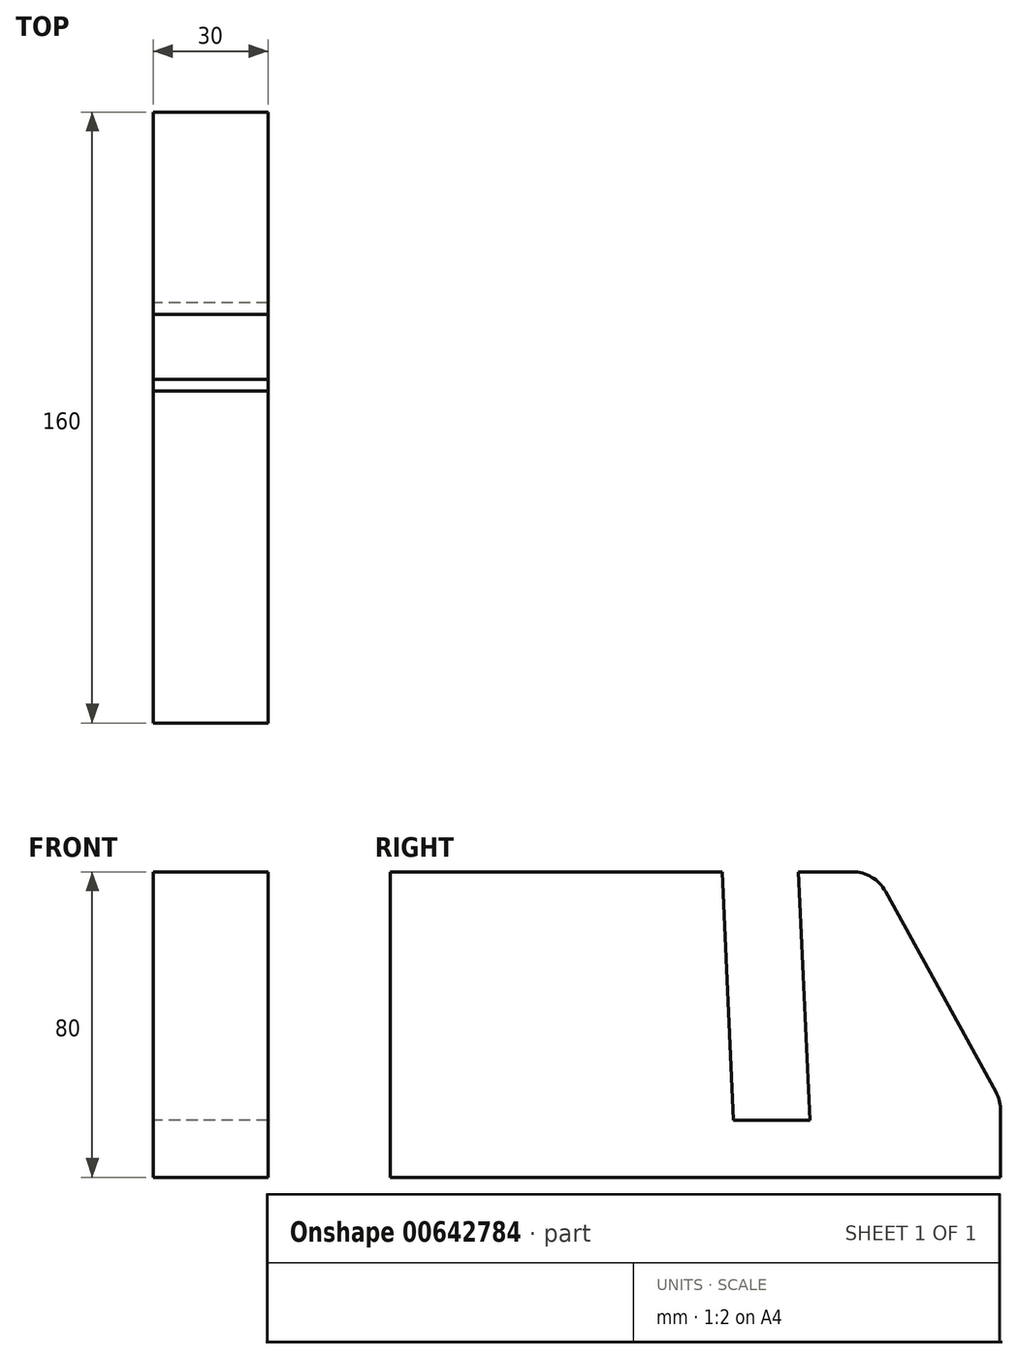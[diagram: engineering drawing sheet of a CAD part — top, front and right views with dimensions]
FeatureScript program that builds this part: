
annotation { "Feature Type Name" : "Feature", "Feature Type Description" : "" }
export const myFeature = defineFeature(function(context is Context, id is Id, definition is map)
    precondition{}
    {
        {
            var Q0;
            Q0=qCreatedBy(makeId("Right.planeOp"),FACE);
            var sketch = newSketch(context, id + "F0", { "sketchPlane" : qUnion([Q0])});
            skLineSegment(sketch, "E0", {"start": v(-50, 0) * mm, "end": v(-70, 0) * mm, "construction": true});
            skLineSegment(sketch, "E1", {"start": v(-160, 0) * mm, "end": v(-160, 65) * mm, "construction": true});
            skLineSegment(sketch, "E2", {"start": v(-160, 65) * mm, "end": v(-73, 65) * mm, "construction": true});
            skLineSegment(sketch, "E3", {"start": v(0, 0) * mm, "end": v(0, 5) * mm, "construction": true});
            skLineSegment(sketch, "E4", {"start": v(-33, 65) * mm, "end": v(-53, 65) * mm, "construction": true});
            skLineSegment(sketch, "E5", {"start": v(-53, 65) * mm, "end": v(-50, 0) * mm, "construction": true});
            skLineSegment(sketch, "E6", {"start": v(-160, 0) * mm, "end": v(-160, -15) * mm});
            skLineSegment(sketch, "E7", {"start": v(-160, -15) * mm, "end": v(0, -15) * mm});
            skLineSegment(sketch, "E8", {"start": v(0, -15) * mm, "end": v(0, 5) * mm});
            skLineSegment(sketch, "E9", {"start": v(-73, 65) * mm, "end": v(-70, 0) * mm});
            skLineSegment(sketch, "E10", {"start": v(-70, 0) * mm, "end": v(-50, 0) * mm});
            skLineSegment(sketch, "E11", {"start": v(-50, 0) * mm, "end": v(-53, 65) * mm});
            skLineSegment(sketch, "E12", {"start": v(-53, 65) * mm, "end": v(-33, 65) * mm});
            skLineSegment(sketch, "E13", {"start": v(-73, 65) * mm, "end": v(-160, 65) * mm});
            skLineSegment(sketch, "E14", {"start": v(-160, 65) * mm, "end": v(-160, 0) * mm});
            skLineSegment(sketch, "E15", {"start": v(0, -15) * mm, "end": v(0, 5) * mm, "construction": true});
            skLineSegment(sketch, "E16", {"start": v(-53, 65) * mm, "end": v(-33, 65) * mm, "construction": true});
            skLineSegment(sketch, "E17", {"start": v(-33, 65) * mm, "end": v(0, 5) * mm});
            skSolve(sketch);
        }
        {
            var Q0;
            Q0 = qSketchRegion(id + "F0", true);
            extrude(context, id + "F1", {"entities" : qUnion([Q0]), "depth" : 30 * mm, "offsetDistance" : 25 * mm});
        }
        {
            var Q0;
            Q0=makeQuery(id+"F1.opExtrude","SWEPT_EDGE",EDGE,{"disambiguationData":[OSD([sQuery(id+"F0.wireOp",EDGE,"E12"),sQuery(id+"F0.wireOp",EDGE,"E17")])]});
            var Q1;
            Q1=makeQuery(id+"F1.opExtrude","SWEPT_EDGE",EDGE,{"disambiguationData":[OSD([sQuery(id+"F0.wireOp",EDGE,"E8"),sQuery(id+"F0.wireOp",EDGE,"E17")])]});
            fillet(context, id + "F2", {"entities" : qUnion([Q0, Q1]), "radius" : 10 * mm, "tangentPropagation" : true, "allowEdgeOverflow" : false});
        }
    });
